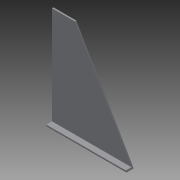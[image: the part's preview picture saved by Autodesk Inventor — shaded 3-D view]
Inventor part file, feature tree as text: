
AUTODESK INVENTOR PART (.ipt)
format: ipt  version: 2013 (Build 170138000, 138)  size: 79,872 bytes
history: native  units: in
note: dims shown in document units (in); Inventor stores cm internally (conversion verified against a paired STEP export)
features: extrude x2, sketch x2
ambient origin geometry x8: Origin, YZ Plane, XZ Plane, XY Plane, X Axis, Y Axis, Z Axis, Center Point
bodies: Solid1 (feature_tree)
feature tree (4):
  extrude  "Extrusion1"  Depth=8.688in
  extrude  "Extrusion2"  Depth=0.125in TaperAngle=0.0deg
  sketch  "Sketch1"  dims[d0=2.0in d1=8.688in]
  sketch  "Sketch2"  dims[d2=60.0deg d3=0.125in d4=0.0in d5=0.125in d6=0.5in d7=0.0in]
